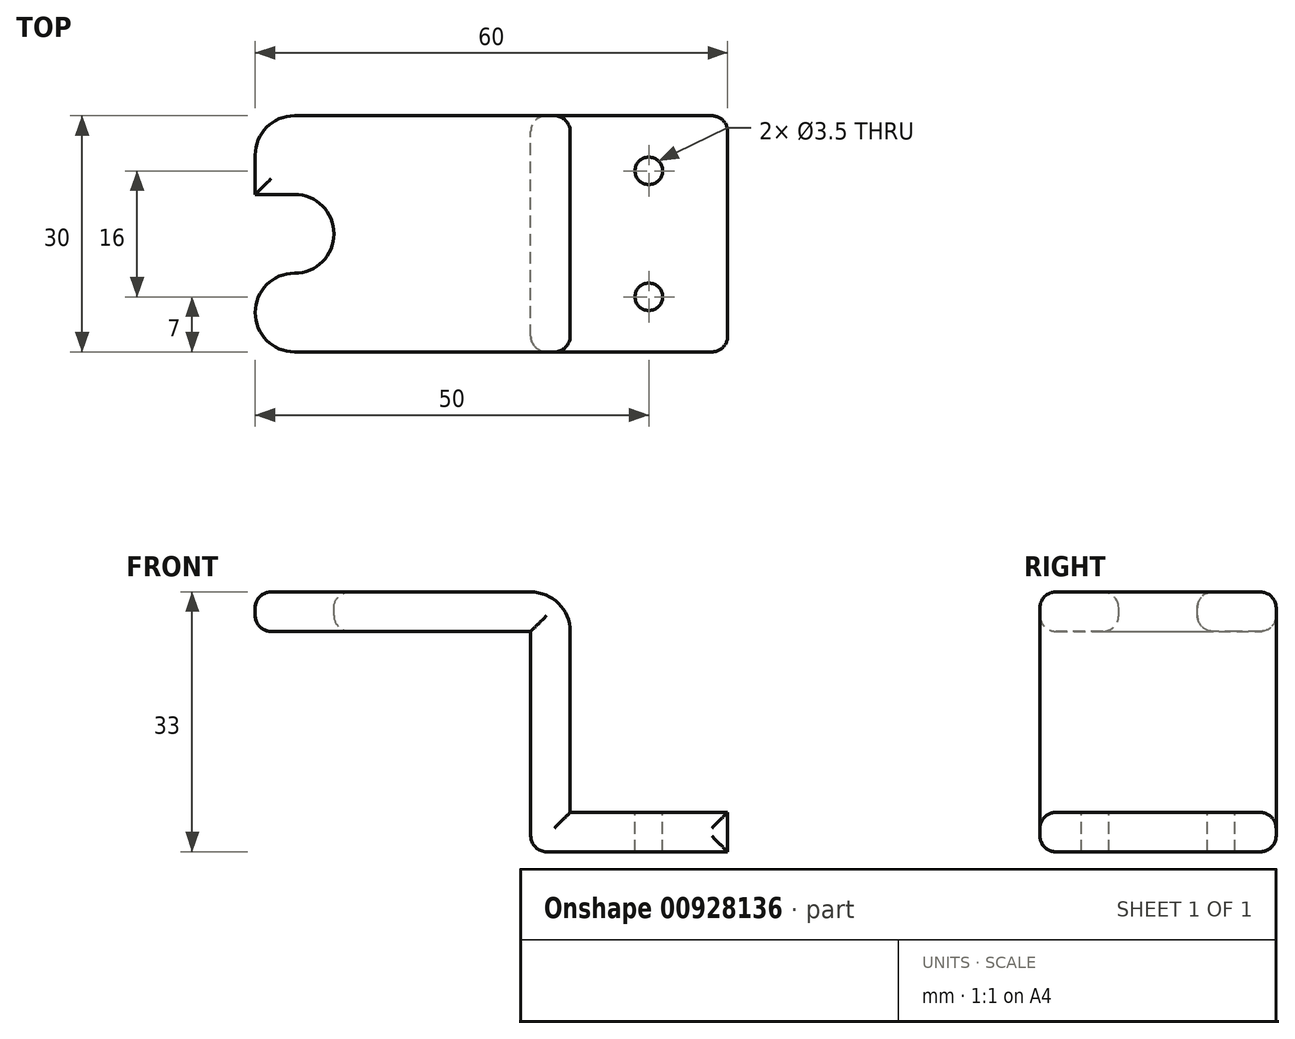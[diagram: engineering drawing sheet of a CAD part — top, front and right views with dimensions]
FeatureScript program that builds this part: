
annotation { "Feature Type Name" : "Feature", "Feature Type Description" : "" }
export const myFeature = defineFeature(function(context is Context, id is Id, definition is map)
    precondition{}
    {
        {
            var Q0;
            Q0=qCreatedBy(makeId("Top.planeOp"),FACE);
            var sketch = newSketch(context, id + "F0", { "sketchPlane" : qUnion([Q0])});
            skLineSegment(sketch, "E0.bottom", {"start": v(-20, 15) * mm, "end": v(20, 15) * mm});
            skLineSegment(sketch, "E0.top", {"start": v(-20, -15) * mm, "end": v(20, -15) * mm});
            skLineSegment(sketch, "E0.left", {"start": v(-20, 15) * mm, "end": v(-20, -15) * mm});
            skLineSegment(sketch, "E0.right", {"start": v(20, 15) * mm, "end": v(20, -15) * mm});
            skPoint(sketch, "E0.middle", {"position": v(0, 0) * mm});
            skSolve(sketch);
        }
        {
            var Q0;
            Q0 = qSketchRegion(id + "F0", true);
            extrude(context, id + "F1", {"entities" : qUnion([Q0]), "depth" : 5 * mm, "offsetDistance" : 25 * mm});
        }
        {
            var Q0;
            Q0=makeQuery(id+"F1.opExtrude","CAP_FACE",FACE,{"disambiguationData":[OSD([sQuery(id+"F0.wireOp",EDGE,"E0.bottom"),sQuery(id+"F0.wireOp",EDGE,"E0.top"),sQuery(id+"F0.wireOp",EDGE,"E0.left"),sQuery(id+"F0.wireOp",EDGE,"E0.right")])],"isStart":false});
            var sketch = newSketch(context, id + "F2", { "sketchPlane" : qUnion([Q0])});
            skLineSegment(sketch, "E1.bottom", {"start": v(-20, 5) * mm, "end": v(-10, 5) * mm});
            skLineSegment(sketch, "E1.top", {"start": v(-20, -5) * mm, "end": v(-10, -5) * mm});
            skLineSegment(sketch, "E1.left", {"start": v(-20, 5) * mm, "end": v(-20, -5) * mm});
            skLineSegment(sketch, "E1.right", {"start": v(-10, 5) * mm, "end": v(-10, -5) * mm});
            skSolve(sketch);
        }
        {
            var Q0;
            Q0=makeQuery(id+"F2.imprint","IMPRINT",FACE,{"disambiguationData":[TD([[makeQuery(id+"F2.imprint","IMPRINT",EDGE,{"derivedFrom":sQuery(id+"F2.wireOp",EDGE,"E1.bottom")}),-1.0]])]});
            extrude(context, id + "F3", {"entities" : qUnion([Q0]), "operationType" : NewBodyOperationType.REMOVE, "oppositeDirection" : true, "depth" : 25 * mm, "offsetDistance" : 25 * mm});
        }
        {
            var Q0;
            Q0=makeQuery(id+"F1.opExtrude","CAP_FACE",FACE,{"disambiguationData":[OSD([sQuery(id+"F0.wireOp",EDGE,"E0.bottom"),sQuery(id+"F0.wireOp",EDGE,"E0.top"),sQuery(id+"F0.wireOp",EDGE,"E0.left"),sQuery(id+"F0.wireOp",EDGE,"E0.right")])],"isStart":true});
            var sketch = newSketch(context, id + "F4", { "sketchPlane" : qUnion([Q0])});
            skLineSegment(sketch, "E2.bottom", {"start": v(20, 15) * mm, "end": v(15, 15) * mm});
            skLineSegment(sketch, "E2.top", {"start": v(20, -15) * mm, "end": v(15, -15) * mm});
            skLineSegment(sketch, "E2.left", {"start": v(20, 15) * mm, "end": v(20, -15) * mm});
            skLineSegment(sketch, "E2.right", {"start": v(15, 15) * mm, "end": v(15, -15) * mm});
            skSolve(sketch);
        }
        {
            var Q0;
            Q0 = qSketchRegion(id + "F4", true);
            extrude(context, id + "F5", {"entities" : qUnion([Q0]), "operationType" : NewBodyOperationType.ADD, "depth" : 28 * mm, "offsetDistance" : 25 * mm});
        }
        {
            var Q0;
            Q0=makeQuery(id+"F5.boolean.opBoolean","MERGE",FACE,{"derivedFrom":[makeQuery(id+"F1.opExtrude","SWEPT_FACE",FACE,{"disambiguationData":[OSD([sQuery(id+"F0.wireOp",EDGE,"E0.right")])]}),makeQuery(id+"F5.opExtrude","SWEPT_FACE",FACE,{"disambiguationData":[OSD([sQuery(id+"F4.wireOp",EDGE,"E2.left")])]})]});
            var sketch = newSketch(context, id + "F6", { "sketchPlane" : qUnion([Q0])});
            skLineSegment(sketch, "E3.bottom", {"start": v(15, -28) * mm, "end": v(-15, -28) * mm});
            skLineSegment(sketch, "E3.top", {"start": v(15, -23) * mm, "end": v(-15, -23) * mm});
            skLineSegment(sketch, "E3.left", {"start": v(15, -28) * mm, "end": v(15, -23) * mm});
            skLineSegment(sketch, "E3.right", {"start": v(-15, -28) * mm, "end": v(-15, -23) * mm});
            skSolve(sketch);
        }
        {
            var Q0;
            Q0 = qSketchRegion(id + "F6", true);
            extrude(context, id + "F7", {"entities" : qUnion([Q0]), "operationType" : NewBodyOperationType.ADD, "depth" : 20 * mm, "offsetDistance" : 25 * mm});
        }
        {
            var Q0;
            Q0=makeQuery(id+"F3.boolean.opBoolean","COPY",EDGE,{"derivedFrom":makeQuery(id+"F3.opExtrude","SWEPT_EDGE",EDGE,{"disambiguationData":[OSD([sQuery(id+"F0.wireOp",EDGE,"E0.left"),sQuery(id+"F2.wireOp",EDGE,"E1.bottom"),sQuery(id+"F2.wireOp",EDGE,"E1.left")])]})});
            var Q1;
            Q1=makeQuery(id+"F3.boolean.opBoolean","COPY",EDGE,{"derivedFrom":makeQuery(id+"F3.opExtrude","SWEPT_EDGE",EDGE,{"disambiguationData":[OSD([sQuery(id+"F0.wireOp",EDGE,"E0.left"),sQuery(id+"F2.wireOp",EDGE,"E1.top"),sQuery(id+"F2.wireOp",EDGE,"E1.left")])]})});
            var Q2;
            Q2=makeQuery(id+"F1.opExtrude","SWEPT_EDGE",EDGE,{"disambiguationData":[OSD([sQuery(id+"F0.wireOp",EDGE,"E0.top"),sQuery(id+"F0.wireOp",EDGE,"E0.left")])]});
            var Q3;
            Q3=makeQuery(id+"F1.opExtrude","SWEPT_EDGE",EDGE,{"disambiguationData":[OSD([sQuery(id+"F0.wireOp",EDGE,"E0.bottom"),sQuery(id+"F0.wireOp",EDGE,"E0.left")])]});
            var Q4;
            Q4=makeQuery(id+"F1.opExtrude","CAP_EDGE",EDGE,{"disambiguationData":[OSD([sQuery(id+"F0.wireOp",EDGE,"E0.right")])],"isStart":false});
            var Q5;
            Q5=makeQuery(id+"F3.boolean.opBoolean","COPY",EDGE,{"derivedFrom":makeQuery(id+"F3.opExtrude","SWEPT_EDGE",EDGE,{"disambiguationData":[OSD([sQuery(id+"F2.wireOp",EDGE,"E1.top"),sQuery(id+"F2.wireOp",EDGE,"E1.right")])]})});
            var Q6;
            Q6=makeQuery(id+"F3.boolean.opBoolean","COPY",EDGE,{"derivedFrom":makeQuery(id+"F3.opExtrude","SWEPT_EDGE",EDGE,{"disambiguationData":[OSD([sQuery(id+"F2.wireOp",EDGE,"E1.bottom"),sQuery(id+"F2.wireOp",EDGE,"E1.right")])]})});
            var Q7;
            Q7=makeQuery(id+"F5.opExtrude","CAP_EDGE",EDGE,{"disambiguationData":[OSD([sQuery(id+"F4.wireOp",EDGE,"E2.right")])],"isStart":true});
            fillet(context, id + "F8", {"entities" : qUnion([Q0, Q1, Q2, Q3, Q4, Q5, Q6, Q7]), "radius" : 5 * mm, "tangentPropagation" : true, "allowEdgeOverflow" : false});
        }
        {
            var Q0;
            Q0=makeQuery(id+"F1.opExtrude","CAP_FACE",FACE,{"disambiguationData":[OSD([sQuery(id+"F0.wireOp",EDGE,"E0.bottom"),sQuery(id+"F0.wireOp",EDGE,"E0.top"),sQuery(id+"F0.wireOp",EDGE,"E0.left"),sQuery(id+"F0.wireOp",EDGE,"E0.right")])],"isStart":false});
            var Q1;
            Q1=makeQuery(id+"F5.opExtrude","SWEPT_EDGE",EDGE,{"disambiguationData":[OSD([sQuery(id+"F0.wireOp",EDGE,"E0.top"),sQuery(id+"F4.wireOp",EDGE,"E2.bottom"),sQuery(id+"F4.wireOp",EDGE,"E2.right")])]});
            var Q2;
            Q2=makeQuery(id+"F5.opExtrude","CAP_EDGE",EDGE,{"disambiguationData":[OSD([sQuery(id+"F4.wireOp",EDGE,"E2.right")])],"isStart":false});
            var Q3;
            Q3=makeQuery(id+"F7.boolean.opBoolean","MERGE",FACE,{"derivedFrom":[makeQuery(id+"F5.boolean.opBoolean","MERGE",FACE,{"derivedFrom":[makeQuery(id+"F1.opExtrude","SWEPT_FACE",FACE,{"disambiguationData":[OSD([sQuery(id+"F0.wireOp",EDGE,"E0.top")])]}),makeQuery(id+"F5.opExtrude","SWEPT_FACE",FACE,{"disambiguationData":[OSD([sQuery(id+"F4.wireOp",EDGE,"E2.bottom")])]})]}),makeQuery(id+"F7.opExtrude","SWEPT_FACE",FACE,{"disambiguationData":[OSD([sQuery(id+"F6.wireOp",EDGE,"E3.right")])]})]});
            var Q4;
            Q4=makeQuery(id+"F7.boolean.opBoolean","MERGE",FACE,{"derivedFrom":[makeQuery(id+"F5.boolean.opBoolean","MERGE",FACE,{"derivedFrom":[makeQuery(id+"F1.opExtrude","SWEPT_FACE",FACE,{"disambiguationData":[OSD([sQuery(id+"F0.wireOp",EDGE,"E0.bottom")])]}),makeQuery(id+"F5.opExtrude","SWEPT_FACE",FACE,{"disambiguationData":[OSD([sQuery(id+"F4.wireOp",EDGE,"E2.top")])]})]}),makeQuery(id+"F7.opExtrude","SWEPT_FACE",FACE,{"disambiguationData":[OSD([sQuery(id+"F6.wireOp",EDGE,"E3.left")])]})]});
            fillet(context, id + "F9", {"entities" : qUnion([Q0, Q1, Q2, Q3, Q4]), "radius" : 2 * mm, "tangentPropagation" : true, "allowEdgeOverflow" : false});
        }
        {
            var Q0;
            Q0=makeQuery(id+"F7.opExtrude","SWEPT_FACE",FACE,{"disambiguationData":[OSD([sQuery(id+"F6.wireOp",EDGE,"E3.top")])]});
            var sketch = newSketch(context, id + "F10", { "sketchPlane" : qUnion([Q0])});
            skPoint(sketch, "E4", {"position": v(30, -8) * mm});
            skPoint(sketch, "E4.positionSnap0", {"position": v(30, -13) * mm});
            skPoint(sketch, "E5", {"position": v(30, 8) * mm});
            skPoint(sketch, "E5.positionSnap0", {"position": v(30, 13) * mm});
            skCircle(sketch, "E6", {"center": v(30, -8) * mm, "radius": 1.75 * mm});
            skCircle(sketch, "E7", {"center": v(30, 8) * mm, "radius": 1.75 * mm});
            skSolve(sketch);
        }
        {
            var Q0;
            Q0=makeQuery(id+"F10.imprint","IMPRINT",FACE,{"disambiguationData":[TD([[makeQuery(id+"F10.imprint","IMPRINT",EDGE,{"derivedFrom":sQuery(id+"F10.wireOp",EDGE,"E6")}),1.0]])]});
            var Q1;
            Q1=makeQuery(id+"F10.imprint","IMPRINT",FACE,{"disambiguationData":[TD([[makeQuery(id+"F10.imprint","IMPRINT",EDGE,{"derivedFrom":sQuery(id+"F10.wireOp",EDGE,"E7")}),1.0]])]});
            extrude(context, id + "F11", {"entities" : qUnion([Q0, Q1]), "operationType" : NewBodyOperationType.REMOVE, "oppositeDirection" : true, "depth" : 25 * mm, "offsetDistance" : 25 * mm});
        }
    });
